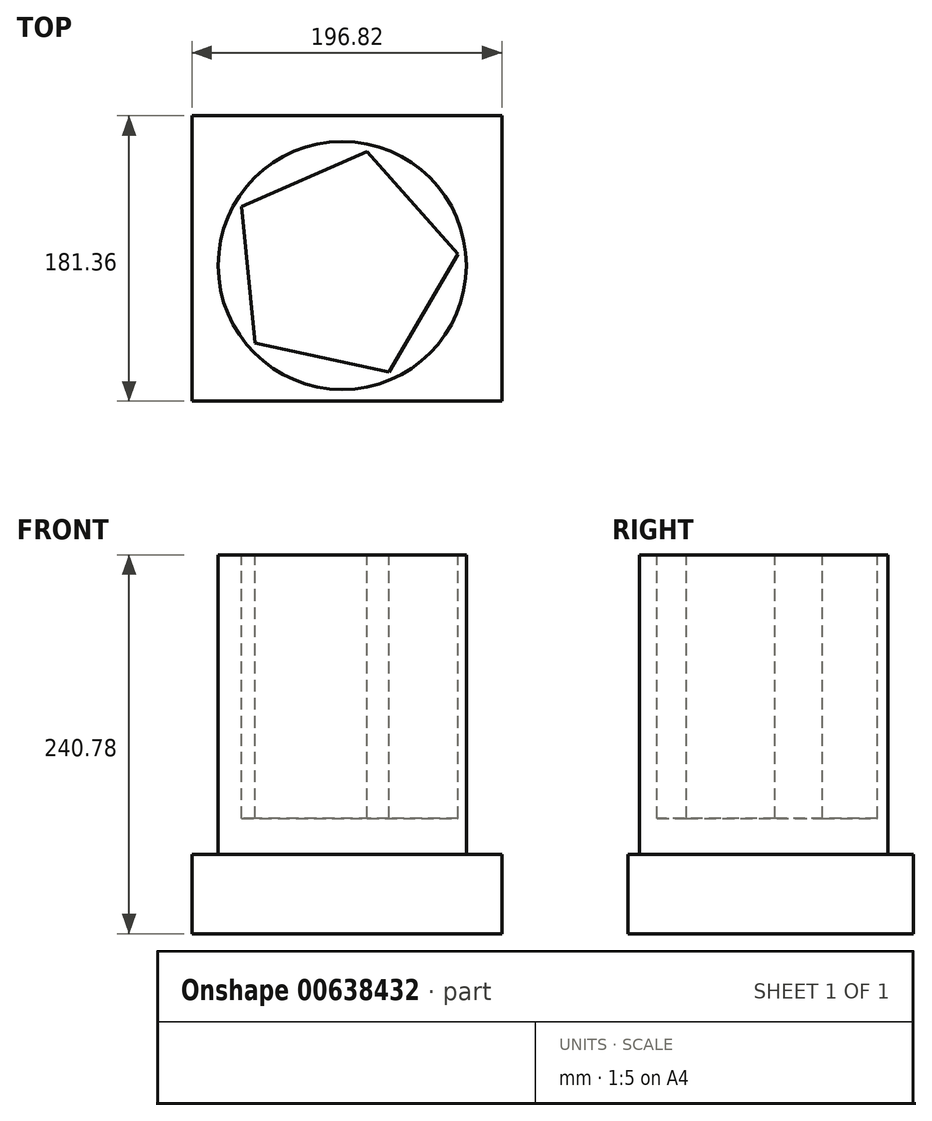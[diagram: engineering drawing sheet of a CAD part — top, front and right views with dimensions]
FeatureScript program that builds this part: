
annotation { "Feature Type Name" : "Feature", "Feature Type Description" : "" }
export const myFeature = defineFeature(function(context is Context, id is Id, definition is map)
    precondition{}
    {
        {
            var Q0;
            Q0=qCreatedBy(makeId("Front.planeOp"),FACE);
            var sketch = newSketch(context, id + "F0", { "sketchPlane" : qUnion([Q0])});
            skLineSegment(sketch, "E0.bottom", {"start": v(56.1, 50.53) * mm, "end": v(0, 50.53) * mm});
            skLineSegment(sketch, "E0.top", {"start": v(56.1, 0) * mm, "end": v(0, 0) * mm});
            skLineSegment(sketch, "E0.left", {"start": v(56.1, 50.53) * mm, "end": v(56.1, 0) * mm});
            skLineSegment(sketch, "E0.right", {"start": v(0, 50.53) * mm, "end": v(0, 0) * mm});
            skSolve(sketch);
        }
        {
            var Q0;
            Q0 = qSketchRegion(id + "F0", true);
            extrude(context, id + "F1", {"entities" : qUnion([Q0]), "depth" : 75.7 * mm, "offsetDistance" : 25.4 * mm});
        }
        {
            var Q0;
            Q0=makeQuery(id+"F1.opExtrude","SWEPT_FACE",FACE,{"disambiguationData":[OSD([sQuery(id+"F0.wireOp",EDGE,"E0.left")])]});
            extrude(context, id + "F2", {"entities" : qUnion([Q0]), "operationType" : NewBodyOperationType.ADD, "depth" : 140.72 * mm, "offsetDistance" : 25.4 * mm});
        }
        {
            var Q0;
            {var subQ0=sQuery(id+"F0.wireOp",EDGE,"E0.left");Q0=makeQuery(id+"F2.boolean.opBoolean","MERGE",FACE,{"derivedFrom":[makeQuery(id+"F1.opExtrude","CAP_FACE",FACE,{"disambiguationData":[OSD([sQuery(id+"F0.wireOp",EDGE,"E0.bottom"),sQuery(id+"F0.wireOp",EDGE,"E0.top"),subQ0,sQuery(id+"F0.wireOp",EDGE,"E0.right")])],"isStart":false}),makeQuery(id+"F2.opExtrude","SWEPT_FACE",FACE,{"disambiguationData":[OSD([subQ0]),TDD([makeQuery(id+"F1.opExtrude","CAP_EDGE",EDGE,{"disambiguationData":[OSD([subQ0])],"isStart":false})])]})]});}
            extrude(context, id + "F3", {"entities" : qUnion([Q0]), "operationType" : NewBodyOperationType.ADD, "depth" : 105.66 * mm, "offsetDistance" : 25.4 * mm});
        }
        {
            var Q0;
            {var subQ0=sQuery(id+"F0.wireOp",EDGE,"E0.left");var subQ1=sQuery(id+"F0.wireOp",EDGE,"E0.bottom");Q0=makeQuery(id+"F3.boolean.opBoolean","MERGE",FACE,{"derivedFrom":[makeQuery(id+"F2.boolean.opBoolean","MERGE",FACE,{"derivedFrom":[makeQuery(id+"F1.opExtrude","SWEPT_FACE",FACE,{"disambiguationData":[OSD([subQ1])]}),makeQuery(id+"F2.opExtrude","SWEPT_FACE",FACE,{"disambiguationData":[OSD([subQ1,subQ0])]})]}),makeQuery(id+"F3.opExtrude","SWEPT_FACE",FACE,{"disambiguationData":[OSD([subQ1,subQ0])]})]});}
            var sketch = newSketch(context, id + "F4", { "sketchPlane" : qUnion([Q0])});
            skCircle(sketch, "E1", {"center": v(95.39, -95.11) * mm, "radius": 78.79 * mm});
            skSolve(sketch);
        }
        {
            var Q0;
            Q0 = qSketchRegion(id + "F4", true);
            extrude(context, id + "F5", {"entities" : qUnion([Q0]), "operationType" : NewBodyOperationType.ADD, "depth" : 190.25 * mm, "offsetDistance" : 25.4 * mm});
        }
        {
            var Q0;
            Q0=makeQuery(id+"F5.opExtrude","CAP_FACE",FACE,{"disambiguationData":[OSD([sQuery(id+"F4.wireOp",EDGE,"E1")])],"isStart":false});
            var sketch = newSketch(context, id + "F6", { "sketchPlane" : qUnion([Q0])});
            skCircle(sketch, "E2", {"center": v(95.39, -95.11) * mm, "radius": 25.29 * mm});
            skSolve(sketch);
        }
        {
            var Q0;
            Q0 = qSketchRegion(id + "F6", true);
            extrude(context, id + "F7", {"entities" : qUnion([Q0]), "operationType" : NewBodyOperationType.REMOVE, "depth" : 125.48 * mm, "offsetDistance" : 25.4 * mm});
        }
        {
            var Q0;
            Q0=makeQuery(id+"F5.opExtrude","CAP_FACE",FACE,{"disambiguationData":[OSD([sQuery(id+"F4.wireOp",EDGE,"E1")])],"isStart":false});
            var sketch = newSketch(context, id + "F8", { "sketchPlane" : qUnion([Q0])});
            skCircle(sketch, "E3", {"center": v(95.39, -95.11) * mm, "radius": 34.62 * mm});
            skSolve(sketch);
        }
        {
            var Q0;
            Q0=makeQuery(id+"F8.imprint","IMPRINT",FACE,{"disambiguationData":[TD([[makeQuery(id+"F8.imprint","IMPRINT",EDGE,{"derivedFrom":sQuery(id+"F8.wireOp",EDGE,"E3")}),1.0]])]});
            extrude(context, id + "F9", {"entities" : qUnion([Q0]), "operationType" : NewBodyOperationType.REMOVE, "oppositeDirection" : true, "depth" : 83.57 * mm, "offsetDistance" : 25.4 * mm});
        }
        {
            var Q0;
            Q0=makeQuery(id+"F5.opExtrude","CAP_FACE",FACE,{"disambiguationData":[OSD([sQuery(id+"F4.wireOp",EDGE,"E1")])],"isStart":false});
            var sketch = newSketch(context, id + "F10", { "sketchPlane" : qUnion([Q0])});
            skCircle(sketch, "E4.cCircle", {"center": v(95.39, -95.11) * mm, "radius": 59.86 * mm, "construction": true});
            skLineSegment(sketch, "E4.0", {"start": v(125.06, -162.89) * mm, "end": v(40.1, -144.27) * mm});
            skLineSegment(sketch, "E4.1", {"start": v(40.1, -144.27) * mm, "end": v(31.55, -57.72) * mm});
            skLineSegment(sketch, "E4.2", {"start": v(31.55, -57.72) * mm, "end": v(111.22, -22.84) * mm});
            skLineSegment(sketch, "E4.3", {"start": v(111.22, -22.84) * mm, "end": v(169.02, -87.84) * mm});
            skLineSegment(sketch, "E4.4", {"start": v(169.02, -87.84) * mm, "end": v(125.06, -162.89) * mm});
            skPoint(sketch, "E4.0.midPoint", {"position": v(82.58, -153.58) * mm});
            skSolve(sketch);
        }
        {
            var Q0;
            Q0 = qSketchRegion(id + "F10", true);
            extrude(context, id + "F11", {"entities" : qUnion([Q0]), "operationType" : NewBodyOperationType.REMOVE, "oppositeDirection" : true, "depth" : 167.39 * mm, "offsetDistance" : 25.4 * mm});
        }
    });
